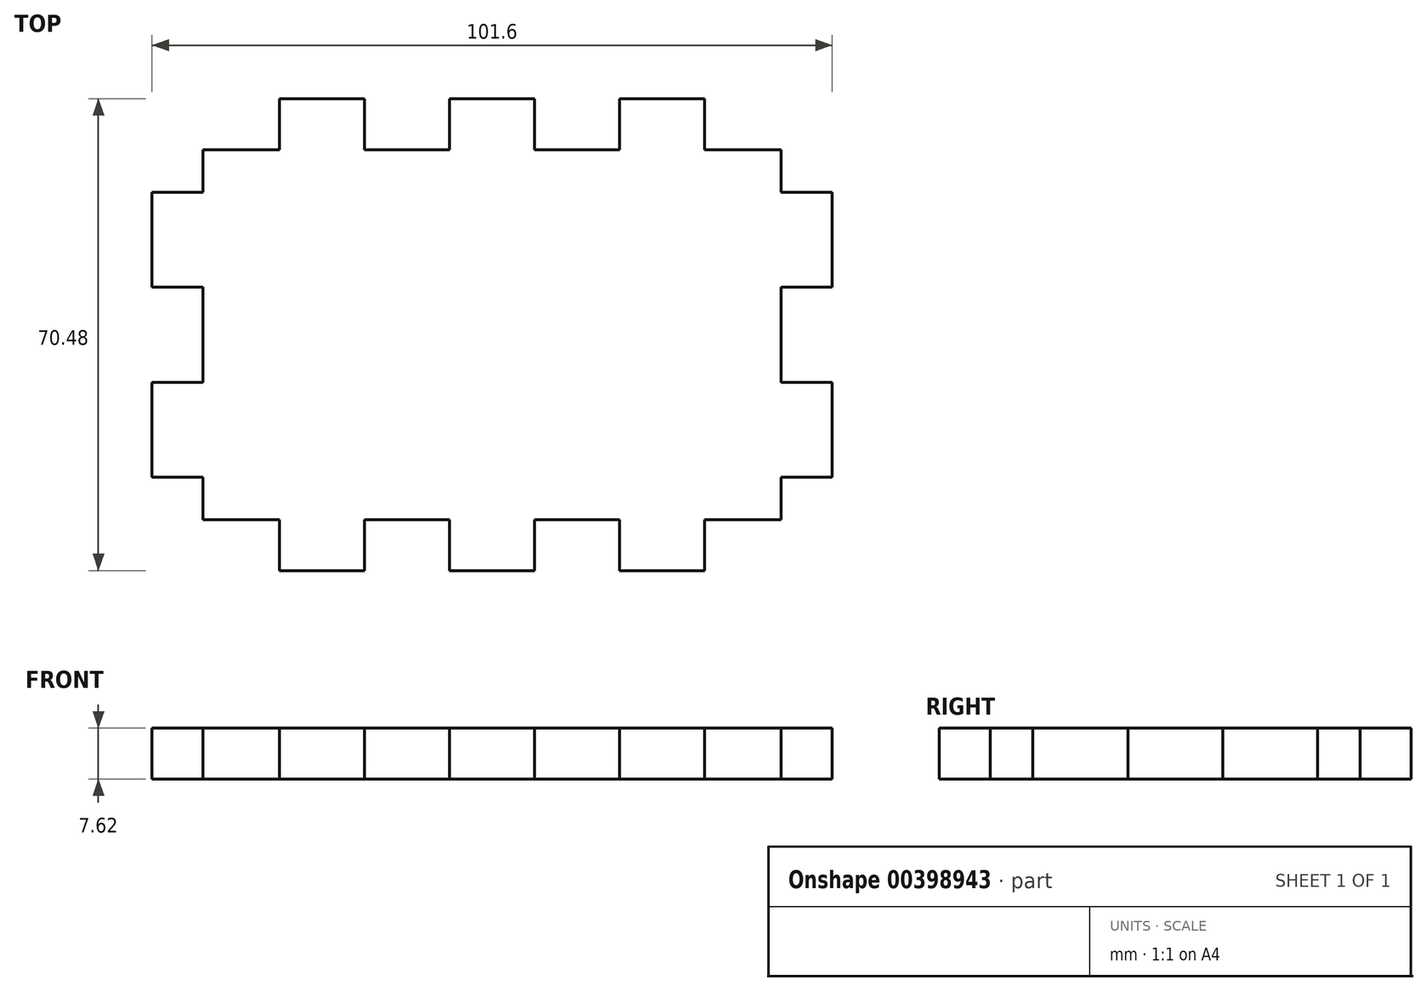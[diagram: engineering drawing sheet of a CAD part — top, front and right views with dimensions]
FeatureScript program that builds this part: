
annotation { "Feature Type Name" : "Feature", "Feature Type Description" : "" }
export const myFeature = defineFeature(function(context is Context, id is Id, definition is map)
    precondition{}
    {
        {
            var Q0;
            Q0=qCreatedBy(makeId("Top.planeOp"),FACE);
            var sketch = newSketch(context, id + "F0", { "sketchPlane" : qUnion([Q0])});
            skLineSegment(sketch, "E0.bottom", {"start": v(19.05, 0) * mm, "end": v(31.75, 0) * mm});
            skLineSegment(sketch, "E1", {"start": v(7.62, -7.62) * mm, "end": v(19.05, -7.62) * mm});
            skLineSegment(sketch, "E2", {"start": v(19.05, -7.62) * mm, "end": v(19.05, 0) * mm});
            skLineSegment(sketch, "E3", {"start": v(31.75, 0) * mm, "end": v(31.75, -7.62) * mm});
            skLineSegment(sketch, "E4", {"start": v(31.75, -7.62) * mm, "end": v(44.45, -7.62) * mm});
            skLineSegment(sketch, "E5", {"start": v(44.45, -7.62) * mm, "end": v(44.45, 0) * mm});
            skLineSegment(sketch, "E6", {"start": v(44.45, 0) * mm, "end": v(57.15, 0) * mm});
            skLineSegment(sketch, "E7", {"start": v(57.15, 0) * mm, "end": v(57.15, -7.62) * mm});
            skLineSegment(sketch, "E8", {"start": v(57.15, -7.62) * mm, "end": v(69.85, -7.62) * mm});
            skLineSegment(sketch, "E9", {"start": v(69.85, -7.62) * mm, "end": v(69.85, 0) * mm});
            skLineSegment(sketch, "E10", {"start": v(69.85, 0) * mm, "end": v(82.55, 0) * mm});
            skLineSegment(sketch, "E11", {"start": v(82.55, 0) * mm, "end": v(82.55, -7.62) * mm});
            skLineSegment(sketch, "E12", {"start": v(82.55, -7.62) * mm, "end": v(93.98, -7.62) * mm});
            skPoint(sketch, "E13.orphan", {"position": v(101.6, 0) * mm});
            skLineSegment(sketch, "E14", {"start": v(7.62, -7.62) * mm, "end": v(7.62, -13.97) * mm});
            skLineSegment(sketch, "E15", {"start": v(7.62, -13.97) * mm, "end": v(0, -13.97) * mm});
            skLineSegment(sketch, "E16", {"start": v(0, -13.97) * mm, "end": v(0, -28.15) * mm});
            skLineSegment(sketch, "E17", {"start": v(0, -28.15) * mm, "end": v(7.62, -28.15) * mm});
            skLineSegment(sketch, "E18", {"start": v(7.62, -28.15) * mm, "end": v(7.62, -42.33) * mm});
            skLineSegment(sketch, "E19", {"start": v(7.62, -42.33) * mm, "end": v(0, -42.33) * mm});
            skLineSegment(sketch, "E20", {"start": v(0, -42.33) * mm, "end": v(0, -56.51) * mm});
            skLineSegment(sketch, "E21", {"start": v(0, -56.51) * mm, "end": v(7.62, -56.51) * mm});
            skLineSegment(sketch, "E22", {"start": v(7.62, -56.51) * mm, "end": v(7.62, -62.86) * mm});
            skPoint(sketch, "E0.left.start.orphan", {"position": v(0, 0) * mm});
            skPoint(sketch, "E23.orphan", {"position": v(0, -70.48) * mm});
            skLineSegment(sketch, "E24", {"start": v(50.8, 0) * mm, "end": v(50.8, -17.84) * mm, "construction": true});
            skLineSegment(sketch, "E25.MirrorCS", {"start": v(93.98, -7.62) * mm, "end": v(93.98, -13.97) * mm});
            skLineSegment(sketch, "E26.MirrorCS", {"start": v(93.98, -13.97) * mm, "end": v(101.6, -13.97) * mm});
            skLineSegment(sketch, "E27.MirrorCS", {"start": v(101.6, -13.97) * mm, "end": v(101.6, -28.15) * mm});
            skLineSegment(sketch, "E28.MirrorCS", {"start": v(101.6, -28.15) * mm, "end": v(93.98, -28.15) * mm});
            skLineSegment(sketch, "E29.MirrorCS", {"start": v(93.98, -28.15) * mm, "end": v(93.98, -42.33) * mm});
            skLineSegment(sketch, "E30.MirrorCS", {"start": v(93.98, -42.33) * mm, "end": v(101.6, -42.33) * mm});
            skLineSegment(sketch, "E31.MirrorCS", {"start": v(101.6, -42.33) * mm, "end": v(101.6, -56.51) * mm});
            skLineSegment(sketch, "E32.MirrorCS", {"start": v(101.6, -56.51) * mm, "end": v(93.98, -56.51) * mm});
            skLineSegment(sketch, "E33.MirrorCS", {"start": v(93.98, -56.51) * mm, "end": v(93.98, -62.86) * mm});
            skLineSegment(sketch, "E34", {"start": v(7.62, -35.24) * mm, "end": v(24.6, -35.24) * mm, "construction": true});
            skLineSegment(sketch, "E35.MirrorCS", {"start": v(7.62, -62.86) * mm, "end": v(19.05, -62.86) * mm});
            skLineSegment(sketch, "E36.MirrorCS", {"start": v(19.05, -62.86) * mm, "end": v(19.05, -70.48) * mm});
            skLineSegment(sketch, "E37.MirrorCS", {"start": v(19.05, -70.48) * mm, "end": v(31.75, -70.48) * mm});
            skLineSegment(sketch, "E38.MirrorCS", {"start": v(31.75, -70.48) * mm, "end": v(31.75, -62.86) * mm});
            skLineSegment(sketch, "E39.MirrorCS", {"start": v(31.75, -62.86) * mm, "end": v(44.45, -62.86) * mm});
            skLineSegment(sketch, "E40.MirrorCS", {"start": v(44.45, -62.86) * mm, "end": v(44.45, -70.48) * mm});
            skLineSegment(sketch, "E41.MirrorCS", {"start": v(44.45, -70.48) * mm, "end": v(57.15, -70.48) * mm});
            skLineSegment(sketch, "E42.MirrorCS", {"start": v(57.15, -70.48) * mm, "end": v(57.15, -62.86) * mm});
            skLineSegment(sketch, "E43.MirrorCS", {"start": v(57.15, -62.86) * mm, "end": v(69.85, -62.86) * mm});
            skLineSegment(sketch, "E44.MirrorCS", {"start": v(69.85, -62.86) * mm, "end": v(69.85, -70.48) * mm});
            skLineSegment(sketch, "E45.MirrorCS", {"start": v(69.85, -70.48) * mm, "end": v(82.55, -70.48) * mm});
            skLineSegment(sketch, "E46.MirrorCS", {"start": v(82.55, -70.48) * mm, "end": v(82.55, -62.86) * mm});
            skLineSegment(sketch, "E47.MirrorCS", {"start": v(82.55, -62.86) * mm, "end": v(93.98, -62.86) * mm});
            skLineSegment(sketch, "E48", {"start": v(0, 0) * mm, "end": v(19.05, 0) * mm, "construction": true});
            skLineSegment(sketch, "E49", {"start": v(0, 0) * mm, "end": v(0, -13.97) * mm, "construction": true});
            skSolve(sketch);
        }
        {
            var Q0;
            Q0=makeQuery(id+"F0.imprint","IMPRINT",FACE,{"disambiguationData":[TD([[makeQuery(id+"F0.imprint","IMPRINT",EDGE,{"derivedFrom":sQuery(id+"F0.wireOp",EDGE,"E1")}),-1.0]])]});
            extrude(context, id + "F1", {"entities" : qUnion([Q0]), "depth" : 7.62 * mm, "offsetDistance" : 25.4 * mm});
        }
    });
